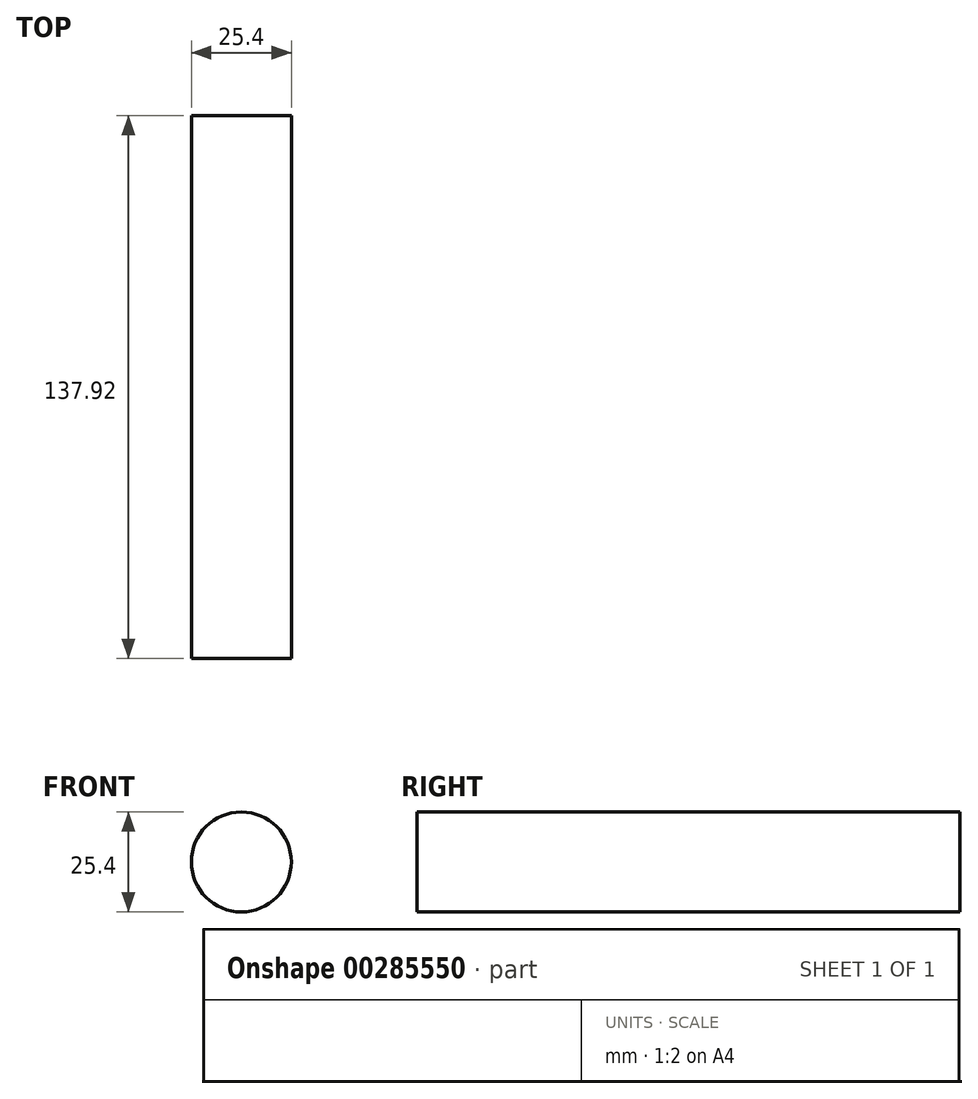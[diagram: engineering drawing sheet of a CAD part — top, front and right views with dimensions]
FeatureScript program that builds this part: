
annotation { "Feature Type Name" : "Feature", "Feature Type Description" : "" }
export const myFeature = defineFeature(function(context is Context, id is Id, definition is map)
    precondition{}
    {
        {
            var Q0;
            Q0=qCreatedBy(makeId("Front.planeOp"),FACE);
            var sketch = newSketch(context, id + "F0", { "sketchPlane" : qUnion([Q0])});
            skCircle(sketch, "E0", {"center": v(0, 0) * mm, "radius": 12.7 * mm});
            skSolve(sketch);
        }
        {
            var Q0;
            Q0 = qSketchRegion(id + "F0", true);
            extrude(context, id + "F1", {"entities" : qUnion([Q0]), "depth" : 137.92 * mm});
        }
    });
